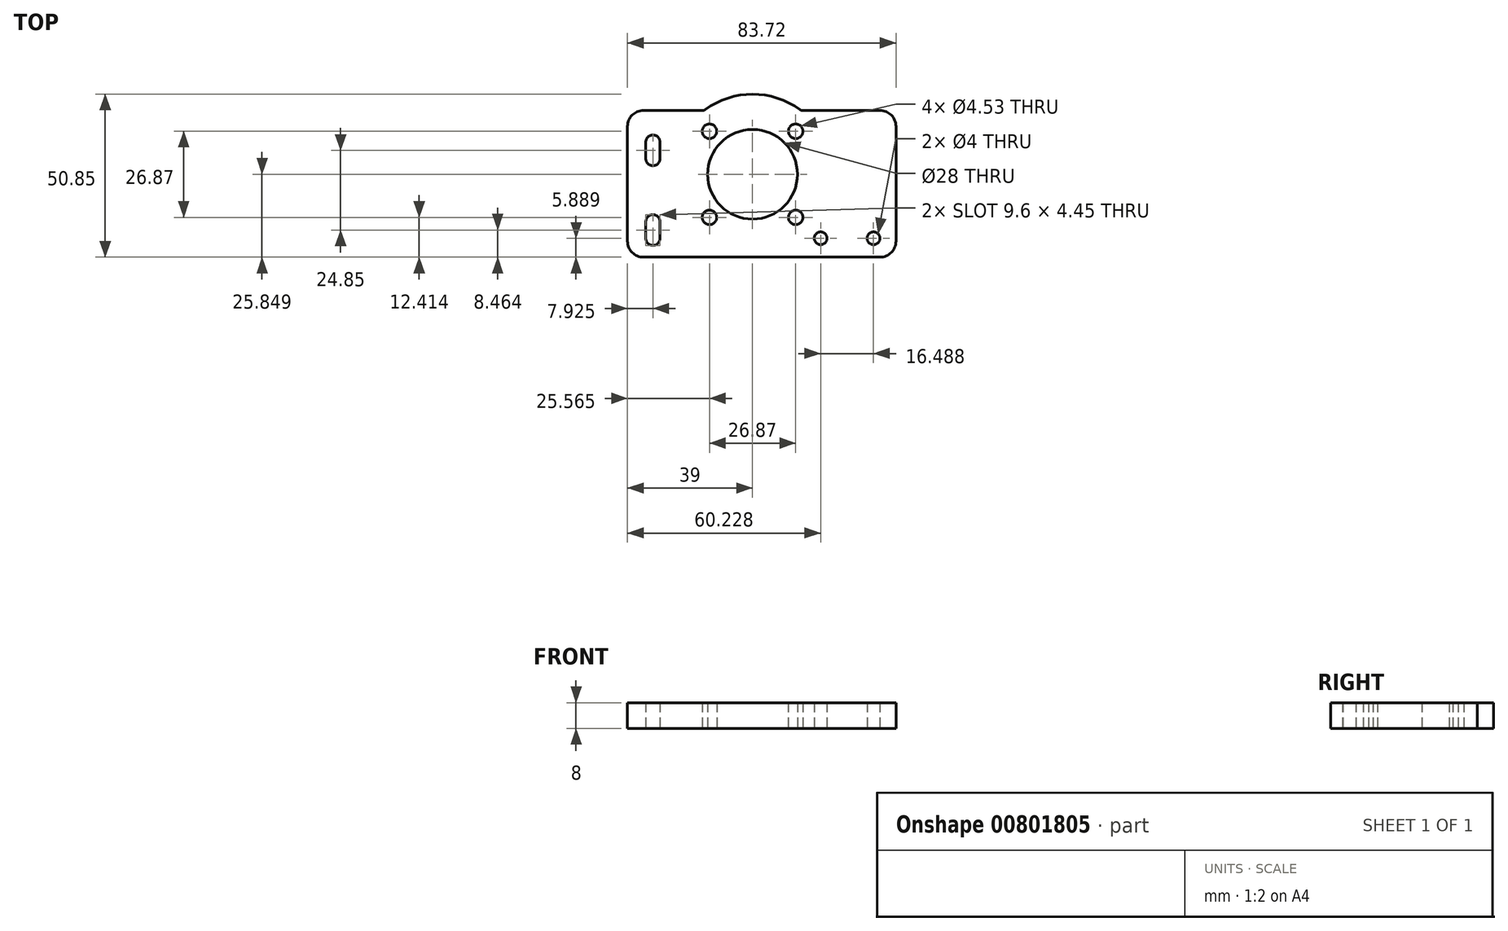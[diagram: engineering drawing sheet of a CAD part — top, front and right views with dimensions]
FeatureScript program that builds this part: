
annotation { "Feature Type Name" : "Feature", "Feature Type Description" : "" }
export const myFeature = defineFeature(function(context is Context, id is Id, definition is map)
    precondition{}
    {
        {
            var Q0;
            Q0=qCreatedBy(makeId("Top.planeOp"),FACE);
            var sketch = newSketch(context, id + "F0", { "sketchPlane" : qUnion([Q0])});
            skLineSegment(sketch, "E0.bottom", {"start": v(-106.95, 1.5) * mm, "end": v(-88.38, 1.5) * mm});
            skLineSegment(sketch, "E0.left", {"start": v(-111.95, -3.5) * mm, "end": v(-111.95, -39.27) * mm});
            skLineSegment(sketch, "E0.right", {"start": v(114.05, -3.5) * mm, "end": v(114.05, -39.27) * mm});
            skLineSegment(sketch, "E1", {"start": v(1.05, 1.5) * mm, "end": v(1.05, -48.27) * mm, "construction": true});
            skCircle(sketch, "E2", {"center": v(1.05, -18.42) * mm, "radius": 5.47 * mm});
            skLineSegment(sketch, "E3", {"start": v(-111.95, -18.42) * mm, "end": v(114.05, -18.42) * mm, "construction": true});
            skPoint(sketch, "E3.endSnap0", {"position": v(114.05, -23.38) * mm});
            skCircle(sketch, "E4", {"center": v(75.05, -18.42) * mm, "radius": 14 * mm});
            skLineSegment(sketch, "E5", {"start": v(106.13, 1.5) * mm, "end": v(106.13, -48.27) * mm, "construction": true});
            skArc(sketch, "E6", {"start": v(108.35, -8.38) * mm, "mid": v(106.13, -6.16) * mm, "end": v(103.9, -8.38) * mm});
            skArc(sketch, "E7", {"start": v(103.9, -13.53) * mm, "mid": v(106.13, -15.76) * mm, "end": v(108.35, -13.53) * mm});
            skLineSegment(sketch, "E8", {"start": v(114.05, -23.38) * mm, "end": v(-111.95, -23.38) * mm, "construction": true});
            skLineSegment(sketch, "E9", {"start": v(103.9, -8.38) * mm, "end": v(108.35, -8.38) * mm, "construction": true});
            skLineSegment(sketch, "E10", {"start": v(103.9, -13.53) * mm, "end": v(108.35, -13.53) * mm, "construction": true});
            skLineSegment(sketch, "E11", {"start": v(103.9, -8.38) * mm, "end": v(103.9, -13.53) * mm});
            skLineSegment(sketch, "E12", {"start": v(108.35, -8.38) * mm, "end": v(108.35, -13.53) * mm});
            skArc(sketch, "E13.MirrorCS", {"start": v(103.9, -33.23) * mm, "mid": v(106.13, -31) * mm, "end": v(108.35, -33.23) * mm});
            skLineSegment(sketch, "E14.MirrorCS", {"start": v(103.9, -38.38) * mm, "end": v(103.9, -33.23) * mm});
            skLineSegment(sketch, "E15.MirrorCS", {"start": v(108.35, -38.38) * mm, "end": v(108.35, -33.23) * mm});
            skArc(sketch, "E16.MirrorCS", {"start": v(108.35, -38.38) * mm, "mid": v(106.13, -40.6) * mm, "end": v(103.9, -38.38) * mm});
            skLineSegment(sketch, "E17.MirrorCS", {"start": v(-101.8, -38.38) * mm, "end": v(-101.8, -33.23) * mm});
            skArc(sketch, "E18.MirrorCS", {"start": v(-106.25, -38.38) * mm, "mid": v(-104.02, -40.6) * mm, "end": v(-101.8, -38.38) * mm});
            skLineSegment(sketch, "E19.MirrorCS", {"start": v(-106.25, -38.38) * mm, "end": v(-106.25, -33.23) * mm});
            skArc(sketch, "E20.MirrorCS", {"start": v(-101.8, -33.23) * mm, "mid": v(-104.02, -31) * mm, "end": v(-106.25, -33.23) * mm});
            skLineSegment(sketch, "E21.MirrorCS", {"start": v(-101.8, -13.53) * mm, "end": v(-106.25, -13.53) * mm, "construction": true});
            skLineSegment(sketch, "E22.MirrorCS", {"start": v(-104.02, 1.5) * mm, "end": v(-104.02, -48.27) * mm, "construction": true});
            skLineSegment(sketch, "E23.MirrorCS", {"start": v(-101.8, -8.38) * mm, "end": v(-106.25, -8.38) * mm, "construction": true});
            skLineSegment(sketch, "E24.MirrorCS", {"start": v(-106.25, -8.38) * mm, "end": v(-106.25, -13.53) * mm});
            skArc(sketch, "E25.MirrorCS", {"start": v(-106.25, -8.38) * mm, "mid": v(-104.02, -6.16) * mm, "end": v(-101.8, -8.38) * mm});
            skLineSegment(sketch, "E26.MirrorCS", {"start": v(-101.8, -8.38) * mm, "end": v(-101.8, -13.53) * mm});
            skArc(sketch, "E27.MirrorCS", {"start": v(-101.8, -13.53) * mm, "mid": v(-104.02, -15.76) * mm, "end": v(-106.25, -13.53) * mm});
            skLineSegment(sketch, "E28", {"start": v(75.05, -18.42) * mm, "end": v(88.49, -31.86) * mm, "construction": true});
            skCircle(sketch, "E29", {"center": v(88.49, -31.86) * mm, "radius": 2.27 * mm});
            skCircle(sketch, "E30.1.0", {"center": v(88.49, -4.99) * mm, "radius": 2.27 * mm});
            skCircle(sketch, "E30.2.0", {"center": v(61.62, -4.99) * mm, "radius": 2.27 * mm});
            skCircle(sketch, "E30.3.0", {"center": v(61.62, -31.86) * mm, "radius": 2.27 * mm});
            skCircle(sketch, "E31.MirrorC", {"center": v(-72.95, -18.42) * mm, "radius": 14 * mm});
            skCircle(sketch, "E32.MirrorC", {"center": v(-86.38, -31.86) * mm, "radius": 2.27 * mm});
            skCircle(sketch, "E33.MirrorC", {"center": v(-59.51, -31.86) * mm, "radius": 2.27 * mm});
            skCircle(sketch, "E34.MirrorC", {"center": v(-59.51, -4.99) * mm, "radius": 2.27 * mm});
            skCircle(sketch, "E35.MirrorC", {"center": v(-86.38, -4.99) * mm, "radius": 2.27 * mm});
            skLineSegment(sketch, "E36", {"start": v(1.05, -18.42) * mm, "end": v(6.53, -18.42) * mm, "construction": true});
            skLineSegment(sketch, "E37", {"start": v(1.05, -18.42) * mm, "end": v(6.65, -24.02) * mm, "construction": true});
            skCircle(sketch, "E38", {"center": v(6.65, -24.02) * mm, "radius": 1.75 * mm});
            skCircle(sketch, "E39.1.0", {"center": v(6.65, -12.83) * mm, "radius": 1.75 * mm});
            skCircle(sketch, "E39.2.0", {"center": v(-4.54, -12.83) * mm, "radius": 1.75 * mm});
            skCircle(sketch, "E39.3.0", {"center": v(-4.54, -24.02) * mm, "radius": 1.75 * mm});
            skPoint(sketch, "E40.visualSharp", {"position": v(-111.95, 1.5) * mm});
            skArc(sketch, "E40.filletArc", {"start": v(-106.95, 1.5) * mm, "mid": v(-110.49, 0.04) * mm, "end": v(-111.95, -3.5) * mm});
            skPoint(sketch, "E41.visualSharp", {"position": v(-111.95, -48.27) * mm});
            skPoint(sketch, "E42.visualSharp", {"position": v(114.05, 1.5) * mm});
            skArc(sketch, "E42.filletArc", {"start": v(114.05, -3.5) * mm, "mid": v(112.59, 0.04) * mm, "end": v(109.05, 1.5) * mm});
            skPoint(sketch, "E43.visualSharp", {"position": v(114.05, -48.27) * mm});
            skArc(sketch, "E44", {"start": v(-58.11, 1.7) * mm, "mid": v(-72.95, 6.58) * mm, "end": v(-87.79, 1.7) * mm});
            skLineSegment(sketch, "E45.trimOffspring", {"start": v(-23.23, 1.5) * mm, "end": v(59.62, 1.5) * mm});
            skLineSegment(sketch, "E46.trimOffspring", {"start": v(-84.72, -44.27) * mm, "end": v(-33.23, -44.27) * mm});
            skArc(sketch, "E47.trimOffspring", {"start": v(89.89, 1.7) * mm, "mid": v(75.05, 6.58) * mm, "end": v(60.21, 1.7) * mm});
            skLineSegment(sketch, "E48.trimOffspring", {"start": v(90.48, 1.5) * mm, "end": v(109.05, 1.5) * mm});
            skPoint(sketch, "E49.visualSharp", {"position": v(-111.95, -69.27) * mm});
            skPoint(sketch, "E50.visualSharp", {"position": v(-95, -69.27) * mm});
            skPoint(sketch, "E51.visualSharp", {"position": v(-85.4, -44.27) * mm});
            skPoint(sketch, "E52.visualSharp", {"position": v(87.5, -44.27) * mm});
            skPoint(sketch, "E53.visualSharp", {"position": v(97.1, -69.27) * mm});
            skPoint(sketch, "E54.visualSharp", {"position": v(114.05, -69.27) * mm});
            skPoint(sketch, "E55.visualSharp", {"position": v(90.15, 1.5) * mm});
            skArc(sketch, "E55.filletArc", {"start": v(89.89, 1.7) * mm, "mid": v(90.17, 1.55) * mm, "end": v(90.48, 1.5) * mm});
            skPoint(sketch, "E56.visualSharp", {"position": v(59.95, 1.5) * mm});
            skArc(sketch, "E56.filletArc", {"start": v(59.62, 1.5) * mm, "mid": v(59.93, 1.55) * mm, "end": v(60.21, 1.7) * mm});
            skPoint(sketch, "E57.visualSharp", {"position": v(-57.85, 1.5) * mm});
            skArc(sketch, "E57.filletArc", {"start": v(-58.11, 1.7) * mm, "mid": v(-57.83, 1.55) * mm, "end": v(-57.52, 1.5) * mm});
            skPoint(sketch, "E58.visualSharp", {"position": v(-88.05, 1.5) * mm});
            skArc(sketch, "E58.filletArc", {"start": v(-88.38, 1.5) * mm, "mid": v(-88.07, 1.55) * mm, "end": v(-87.79, 1.7) * mm});
            skLineSegment(sketch, "E59", {"start": v(-84.72, -44.27) * mm, "end": v(-106.95, -44.27) * mm});
            skLineSegment(sketch, "E60", {"start": v(86.82, -44.27) * mm, "end": v(109.05, -44.27) * mm});
            skPoint(sketch, "E61.visualSharp", {"position": v(114.05, -44.27) * mm});
            skArc(sketch, "E61.filletArc", {"start": v(109.05, -44.27) * mm, "mid": v(112.59, -42.8) * mm, "end": v(114.05, -39.27) * mm});
            skPoint(sketch, "E62.visualSharp", {"position": v(-111.95, -44.27) * mm});
            skArc(sketch, "E62.filletArc", {"start": v(-111.95, -39.27) * mm, "mid": v(-110.49, -42.8) * mm, "end": v(-106.95, -44.27) * mm});
            skCircle(sketch, "E63", {"center": v(1.05, -5.22) * mm, "radius": 2 * mm});
            skCircle(sketch, "E64", {"center": v(1.05, -31.62) * mm, "radius": 2 * mm});
            skLineSegment(sketch, "E65", {"start": v(-104.02, -38.38) * mm, "end": v(106.13, -38.38) * mm, "construction": true});
            skCircle(sketch, "E66", {"center": v(75.05, -18.42) * mm, "radius": 25 * mm, "construction": true});
            skCircle(sketch, "E67", {"center": v(-72.95, -18.42) * mm, "radius": 25 * mm, "construction": true});
            skLineSegment(sketch, "E68", {"start": v(-57.52, 1.5) * mm, "end": v(-33.23, 1.5) * mm});
            skLineSegment(sketch, "E69", {"start": v(-28.23, -3.5) * mm, "end": v(-28.23, -39.27) * mm});
            skPoint(sketch, "E70.newPointA", {"position": v(1.05, 1.5) * mm});
            skPoint(sketch, "E70.newPointB", {"position": v(-28.23, 1.5) * mm});
            skArc(sketch, "E70.filletArc", {"start": v(-28.23, -3.5) * mm, "mid": v(-29.7, 0.04) * mm, "end": v(-33.23, 1.5) * mm});
            skLineSegment(sketch, "E71", {"start": v(-28.23, -3.5) * mm, "end": v(-28.23, 1.5) * mm});
            skArc(sketch, "E72.filletArc", {"start": v(-23.23, 1.5) * mm, "mid": v(-26.77, 0.04) * mm, "end": v(-28.23, -3.5) * mm});
            skArc(sketch, "E73.filletArc", {"start": v(-33.23, -44.27) * mm, "mid": v(-29.7, -42.8) * mm, "end": v(-28.23, -39.27) * mm});
            skLineSegment(sketch, "E74", {"start": v(-23.23, -44.27) * mm, "end": v(86.82, -44.27) * mm});
            skLineSegment(sketch, "E75", {"start": v(-28.23, -39.27) * mm, "end": v(-28.23, -39.27) * mm});
            skArc(sketch, "E76.filletArc", {"start": v(-28.23, -39.27) * mm, "mid": v(-26.77, -42.8) * mm, "end": v(-23.23, -44.27) * mm});
            skLineSegment(sketch, "E77", {"start": v(-59.51, -4.99) * mm, "end": v(61.62, -4.99) * mm, "construction": true});
            skCircle(sketch, "E78", {"center": v(-51.72, -38.38) * mm, "radius": 2 * mm});
            skCircle(sketch, "E79", {"center": v(-35.23, -38.38) * mm, "radius": 2 * mm});
            skSolve(sketch);
        }
        {
            var Q0;
            Q0=makeQuery(id+"F0.imprint","IMPRINT",FACE,{"disambiguationData":[TD([[makeQuery(id+"F0.imprint","IMPRINT",EDGE,{"derivedFrom":sQuery(id+"F0.wireOp",EDGE,"E0.bottom")}),-1.0]])]});
            extrude(context, id + "F1", {"entities" : qUnion([Q0]), "depth" : 8 * mm, "offsetDistance" : 25 * mm});
        }
    });
